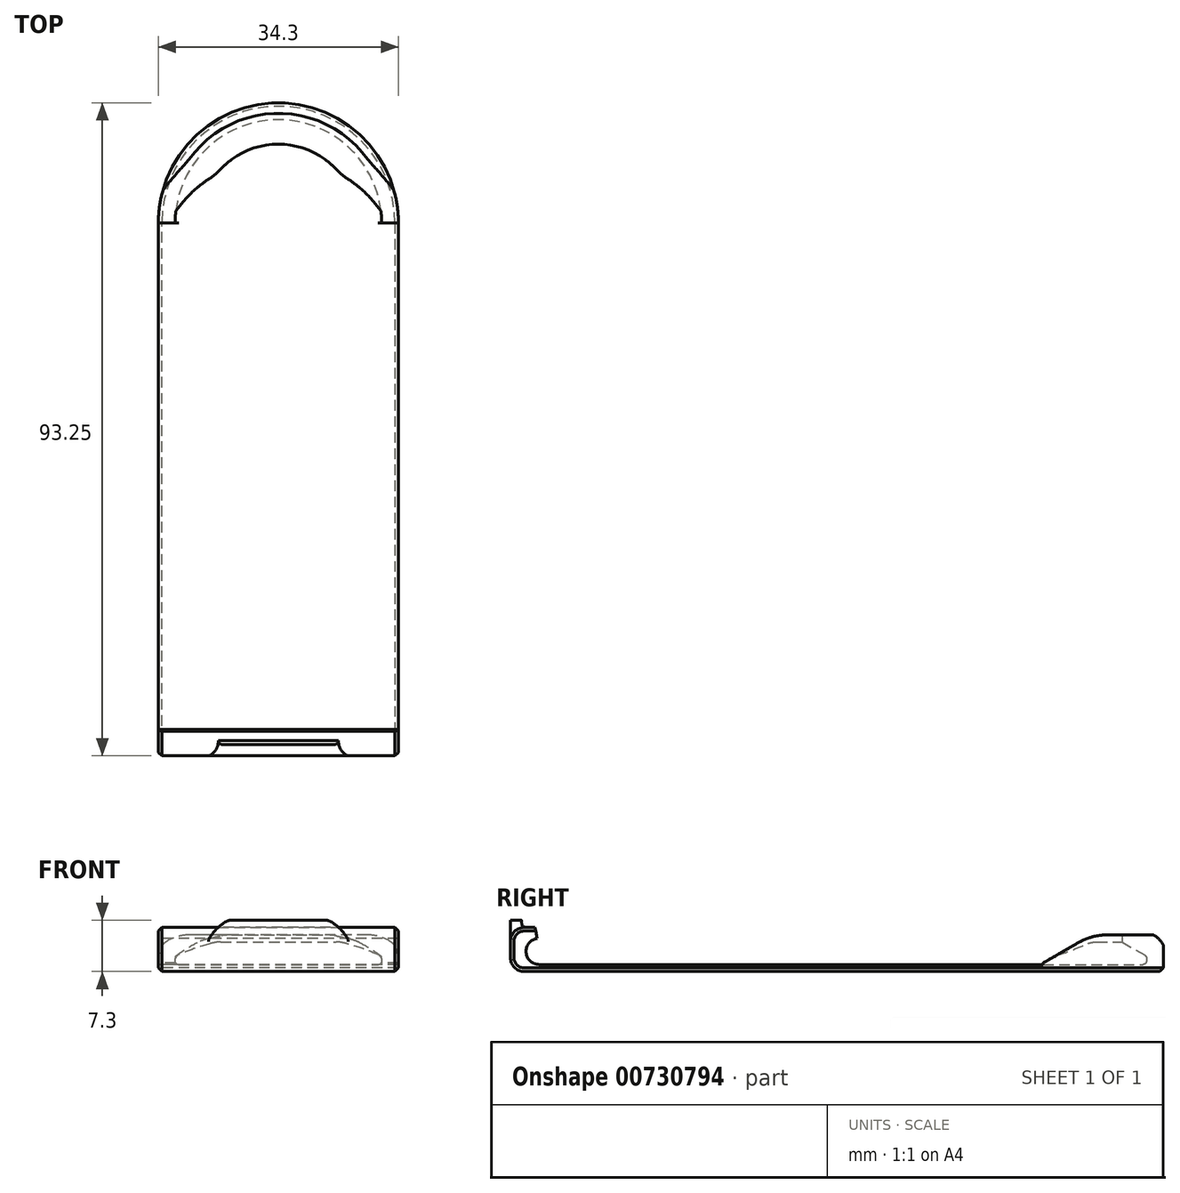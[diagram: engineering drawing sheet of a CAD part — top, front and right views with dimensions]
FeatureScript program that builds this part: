
annotation { "Feature Type Name" : "Feature", "Feature Type Description" : "" }
export const myFeature = defineFeature(function(context is Context, id is Id, definition is map)
    precondition{}
    {
        {
            var Q0;
            Q0=qCreatedBy(makeId("Front.planeOp"),FACE);
            var sketch = newSketch(context, id + "F0", { "sketchPlane" : qUnion([Q0])});
            skLineSegment(sketch, "E0", {"start": v(0, 0) * mm, "end": v(0, 1) * mm});
            skLineSegment(sketch, "E1", {"start": v(0, 1) * mm, "end": v(14.75, 1) * mm});
            skLineSegment(sketch, "E2", {"start": v(14.75, 1) * mm, "end": v(14.75, 2.2) * mm});
            skLineSegment(sketch, "E3", {"start": v(14.75, 2.2) * mm, "end": v(11.25, 4.22) * mm});
            skLineSegment(sketch, "E4", {"start": v(11.25, 4.22) * mm, "end": v(11.25, 5.22) * mm});
            skLineSegment(sketch, "E5", {"start": v(11.25, 5.22) * mm, "end": v(17.15, 5.22) * mm});
            skLineSegment(sketch, "E6", {"start": v(17.15, 5.22) * mm, "end": v(17.15, 0) * mm});
            skLineSegment(sketch, "E7", {"start": v(17.15, 0) * mm, "end": v(0, 0) * mm});
            skSolve(sketch);
        }
        {
            var Q0;
            Q0=makeQuery(id+"F0.imprint","IMPRINT",FACE,{"disambiguationData":[TD([[makeQuery(id+"F0.imprint","IMPRINT",EDGE,{"derivedFrom":sQuery(id+"F0.wireOp",EDGE,"E0")}),-1.0]])]});
            var Q1;
            Q1=sQuery(id+"F0.wireOp",EDGE,"E0");
            revolve(context, id + "F1", {"surfaceOperationType" : NewSurfaceOperationType.NEW, "entities" : qUnion([Q0]), "axis" : qUnion([Q1]), "revolveType" : RevolveType.ONE_DIRECTION, "angle" : 180 * degree});
        }
        {
            var Q0;
            Q0=qCreatedBy(makeId("Top.planeOp"),FACE);
            var sketch = newSketch(context, id + "F2", { "sketchPlane" : qUnion([Q0])});
            skLineSegment(sketch, "E8.bottom", {"start": v(-17.15, 0) * mm, "end": v(17.15, 0) * mm});
            skLineSegment(sketch, "E8.top", {"start": v(-17.15, -72) * mm, "end": v(17.15, -72) * mm});
            skLineSegment(sketch, "E8.left", {"start": v(-17.15, 0) * mm, "end": v(-17.15, -72) * mm});
            skLineSegment(sketch, "E8.right", {"start": v(17.15, 0) * mm, "end": v(17.15, -72) * mm});
            skSolve(sketch);
        }
        {
            var Q0;
            Q0=makeQuery(id+"F2.imprint","IMPRINT",FACE,{"disambiguationData":[TD([[makeQuery(id+"F2.imprint","IMPRINT",EDGE,{"derivedFrom":sQuery(id+"F2.wireOp",EDGE,"E8.bottom")}),-1.0]])]});
            var Q1;
            Q1=makeQuery(id+"F1.opRevolve","SWEPT_FACE",FACE,{"disambiguationData":[OSD([sQuery(id+"F0.wireOp",EDGE,"E1")])]});
            extrude(context, id + "F3", {"entities" : qUnion([Q0]), "operationType" : NewBodyOperationType.ADD, "endBound" : BoundingType.UP_TO_SURFACE, "depth" : 25 * mm, "endBoundEntityFace" : qUnion([Q1]), "offsetDistance" : 25 * mm});
        }
        {
            var Q0;
            {var subQ0=sQuery(id+"F0.wireOp",EDGE,"E1");Q0=makeQuery(id+"F3.boolean.opBoolean","MERGE",FACE,{"derivedFrom":[makeQuery(id+"F1.opRevolve","SWEPT_FACE",FACE,{"disambiguationData":[OSD([subQ0])]}),makeQuery(id+"F3.opExtrude","CAP_FACE",FACE,{"disambiguationData":[OSD([subQ0])],"isStart":false})]});}
            var sketch = newSketch(context, id + "F4", { "sketchPlane" : qUnion([Q0])});
            skCircle(sketch, "E9", {"center": v(0, 0) * mm, "radius": 14.75 * mm, "construction": true});
            skSolve(sketch);
        }
        {
            var Q0;
            Q0=makeQuery(id+"F1.opRevolve","CAP_EDGE",EDGE,{"disambiguationData":[OSD([sQuery(id+"F0.wireOp",EDGE,"E5")])],"isStart":false});
            var Q1;
            Q1=makeQuery(id+"F1.opRevolve","CAP_EDGE",EDGE,{"disambiguationData":[OSD([sQuery(id+"F0.wireOp",EDGE,"E5")])],"isStart":true});
            chamfer(context, id + "F5", {"entities" : qUnion([Q0, Q1]), "chamferType" : ChamferType.OFFSET_ANGLE, "width" : 4 * mm, "oppositeDirection" : false, "angle" : 60 * degree, "tangentPropagation" : true});
        }
        {
            var Q0;
            Q0=makeQuery(id+"F1.opRevolve","SWEPT_FACE",FACE,{"disambiguationData":[OSD([sQuery(id+"F0.wireOp",EDGE,"E5")])]});
            var sketch = newSketch(context, id + "F6", { "sketchPlane" : qUnion([Q0])});
            skArc(sketch, "E10", {"start": v(14.65, 1.7) * mm, "mid": v(0, 9.27) * mm, "end": v(-14.65, 1.7) * mm});
            skLineSegment(sketch, "E11", {"start": v(-14.65, 1.7) * mm, "end": v(14.65, 1.7) * mm});
            skSolve(sketch);
        }
        {
            var Q0;
            Q0 = qSketchRegion(id + "F6", true);
            var Q1;
            {var subQ0=sQuery(id+"F0.wireOp",EDGE,"E1");Q1=makeQuery(id+"F3.boolean.opBoolean","MERGE",FACE,{"derivedFrom":[makeQuery(id+"F1.opRevolve","SWEPT_FACE",FACE,{"disambiguationData":[OSD([subQ0])]}),makeQuery(id+"F3.opExtrude","CAP_FACE",FACE,{"disambiguationData":[OSD([subQ0])],"isStart":false})]});}
            extrude(context, id + "F7", {"entities" : qUnion([Q0]), "operationType" : NewBodyOperationType.REMOVE, "endBound" : BoundingType.UP_TO_SURFACE, "oppositeDirection" : true, "depth" : 25 * mm, "endBoundEntityFace" : qUnion([Q1]), "offsetDistance" : 25 * mm});
        }
        {
            var Q0;
            Q0=makeQuery(id+"F1.opRevolve","SWEPT_EDGE",EDGE,{"disambiguationData":[OSD([sQuery(id+"F0.wireOp",EDGE,"E2"),sQuery(id+"F0.wireOp",EDGE,"E3")])]});
            var Q1;
            Q1=makeQuery(id+"F1.opRevolve","SWEPT_EDGE",EDGE,{"disambiguationData":[OSD([sQuery(id+"F0.wireOp",EDGE,"E1"),sQuery(id+"F0.wireOp",EDGE,"E2")])]});
            fillet(context, id + "F8", {"entities" : qUnion([Q0, Q1]), "radius" : .5 * mm, "allowEdgeOverflow" : false});
        }
        {
            var Q0;
            Q0=makeQuery(id+"F3.opExtrude","SWEPT_FACE",FACE,{"disambiguationData":[OSD([sQuery(id+"F2.wireOp",EDGE,"E8.left")])]});
            var sketch = newSketch(context, id + "F9", { "sketchPlane" : qUnion([Q0])});
            skArc(sketch, "E12", {"start": v(72, 1) * mm, "mid": v(73.87, 2.71) * mm, "end": v(72.33, 4.72) * mm});
            skLineSegment(sketch, "E13", {"start": v(72.33, 4.72) * mm, "end": v(72.6, 6.3) * mm});
            skLineSegment(sketch, "E14", {"start": v(72.6, 6.3) * mm, "end": v(76.1, 6.3) * mm});
            skLineSegment(sketch, "E15", {"start": v(76.1, 6.3) * mm, "end": v(76.1, 0) * mm});
            skLineSegment(sketch, "E16", {"start": v(76.1, 0) * mm, "end": v(72, 0) * mm});
            skLineSegment(sketch, "E17", {"start": v(72, 0) * mm, "end": v(72, 1) * mm});
            skSolve(sketch);
        }
        {
            var Q0;
            Q0 = qSketchRegion(id + "F9", true);
            var Q1;
            Q1=makeQuery(id+"F3.opExtrude","SWEPT_FACE",FACE,{"disambiguationData":[OSD([sQuery(id+"F2.wireOp",EDGE,"E8.right")])]});
            extrude(context, id + "F10", {"entities" : qUnion([Q0]), "operationType" : NewBodyOperationType.ADD, "endBound" : BoundingType.UP_TO_SURFACE, "oppositeDirection" : true, "depth" : 25 * mm, "endBoundEntityFace" : qUnion([Q1]), "offsetDistance" : 25 * mm});
        }
        {
            var Q0;
            Q0=makeQuery(id+"F10.opExtrude","SWEPT_EDGE",EDGE,{"disambiguationData":[OSD([sQuery(id+"F9.wireOp",EDGE,"E14"),sQuery(id+"F9.wireOp",EDGE,"E15")])]});
            var Q1;
            Q1=makeQuery(id+"F10.opExtrude","SWEPT_EDGE",EDGE,{"disambiguationData":[OSD([sQuery(id+"F9.wireOp",EDGE,"E15"),sQuery(id+"F9.wireOp",EDGE,"E16")])]});
            fillet(context, id + "F11", {"entities" : qUnion([Q0, Q1]), "radius" : 2 * mm, "tangentPropagation" : true, "allowEdgeOverflow" : false});
        }
        {
            var Q0;
            Q0=makeQuery(id+"F1.opRevolve","SWEPT_EDGE",EDGE,{"disambiguationData":[OSD([sQuery(id+"F0.wireOp",EDGE,"E5"),sQuery(id+"F0.wireOp",EDGE,"E6")])]});
            fillet(context, id + "F12", {"entities" : qUnion([Q0]), "radius" : 1.5 * mm, "tangentPropagation" : true, "rho" : .2, "crossSection" : FilletCrossSection.CONIC, "allowEdgeOverflow" : false});
        }
        {
            var Q0;
            {var subQ0=sQuery(id+"F0.wireOp",EDGE,"E5");Q0=makeQuery(id+"F5.opChamfer","BLEND_EDGE",EDGE,{"blendedFrom":[makeQuery(id+"F1.opRevolve","CAP_EDGE",EDGE,{"disambiguationData":[OSD([subQ0])],"isStart":true}),makeQuery(id+"F1.opRevolve","SWEPT_FACE",FACE,{"disambiguationData":[OSD([subQ0])]})],"blendedInto":[makeQuery(id+"F1.opRevolve","SWEPT_FACE",FACE,{"disambiguationData":[OSD([subQ0])]})]});}
            var Q1;
            {var subQ0=sQuery(id+"F0.wireOp",EDGE,"E1");Q1=makeQuery(id+"F5.opChamfer","BLEND_EDGE",EDGE,{"blendedFrom":[makeQuery(id+"F1.opRevolve","CAP_EDGE",EDGE,{"disambiguationData":[OSD([sQuery(id+"F0.wireOp",EDGE,"E5")])],"isStart":true}),makeQuery(id+"F3.boolean.opBoolean","MERGE",FACE,{"derivedFrom":[makeQuery(id+"F1.opRevolve","SWEPT_FACE",FACE,{"disambiguationData":[OSD([subQ0])]}),makeQuery(id+"F3.opExtrude","CAP_FACE",FACE,{"disambiguationData":[OSD([subQ0])],"isStart":false})]})],"blendedInto":[makeQuery(id+"F3.boolean.opBoolean","MERGE",FACE,{"derivedFrom":[makeQuery(id+"F1.opRevolve","SWEPT_FACE",FACE,{"disambiguationData":[OSD([subQ0])]}),makeQuery(id+"F3.opExtrude","CAP_FACE",FACE,{"disambiguationData":[OSD([subQ0])],"isStart":false})]})]});}
            var Q2;
            {var subQ0=sQuery(id+"F0.wireOp",EDGE,"E1");Q2=makeQuery(id+"F5.opChamfer","BLEND_EDGE",EDGE,{"blendedFrom":[makeQuery(id+"F1.opRevolve","CAP_EDGE",EDGE,{"disambiguationData":[OSD([sQuery(id+"F0.wireOp",EDGE,"E5")])],"isStart":false}),makeQuery(id+"F3.boolean.opBoolean","MERGE",FACE,{"derivedFrom":[makeQuery(id+"F1.opRevolve","SWEPT_FACE",FACE,{"disambiguationData":[OSD([subQ0])]}),makeQuery(id+"F3.opExtrude","CAP_FACE",FACE,{"disambiguationData":[OSD([subQ0])],"isStart":false})]})],"blendedInto":[makeQuery(id+"F3.boolean.opBoolean","MERGE",FACE,{"derivedFrom":[makeQuery(id+"F1.opRevolve","SWEPT_FACE",FACE,{"disambiguationData":[OSD([subQ0])]}),makeQuery(id+"F3.opExtrude","CAP_FACE",FACE,{"disambiguationData":[OSD([subQ0])],"isStart":false})]})]});}
            var Q3;
            {var subQ0=sQuery(id+"F0.wireOp",EDGE,"E5");Q3=makeQuery(id+"F5.opChamfer","BLEND_EDGE",EDGE,{"blendedFrom":[makeQuery(id+"F1.opRevolve","CAP_EDGE",EDGE,{"disambiguationData":[OSD([subQ0])],"isStart":false}),makeQuery(id+"F1.opRevolve","SWEPT_FACE",FACE,{"disambiguationData":[OSD([subQ0])]})],"blendedInto":[makeQuery(id+"F1.opRevolve","SWEPT_FACE",FACE,{"disambiguationData":[OSD([subQ0])]})]});}
            var Q4;
            Q4=makeQuery(id+"F7.boolean.opBoolean","INTERSECT",EDGE,{"disambiguationData":[OD(1.0)],"derivedFrom":[makeQuery(id+"F1.opRevolve","SWEPT_FACE",FACE,{"disambiguationData":[OSD([sQuery(id+"F0.wireOp",EDGE,"E4")])]}),makeQuery(id+"F7.opExtrude","SWEPT_FACE",FACE,{"disambiguationData":[OSD([sQuery(id+"F6.wireOp",EDGE,"E10")])]})]});
            var Q5;
            Q5=makeQuery(id+"F7.boolean.opBoolean","INTERSECT",EDGE,{"disambiguationData":[OD(0.0)],"derivedFrom":[makeQuery(id+"F1.opRevolve","SWEPT_FACE",FACE,{"disambiguationData":[OSD([sQuery(id+"F0.wireOp",EDGE,"E4")])]}),makeQuery(id+"F7.opExtrude","SWEPT_FACE",FACE,{"disambiguationData":[OSD([sQuery(id+"F6.wireOp",EDGE,"E10")])]})]});
            fillet(context, id + "F13", {"entities" : qUnion([Q0, Q1, Q2, Q3, Q4, Q5]), "radius" : 8 * mm, "allowEdgeOverflow" : false});
        }
        {
            var Q0;
            Q0=makeQuery(id+"F10.opExtrude","SWEPT_FACE",FACE,{"disambiguationData":[OSD([sQuery(id+"F9.wireOp",EDGE,"E15")])]});
            var sketch = newSketch(context, id + "F14", { "sketchPlane" : qUnion([Q0])});
            skLineSegment(sketch, "E18", {"start": v(-10, 4.3) * mm, "end": v(-10, 7.3) * mm});
            skLineSegment(sketch, "E19", {"start": v(-10, 7.3) * mm, "end": v(10, 7.3) * mm});
            skLineSegment(sketch, "E20", {"start": v(10, 7.3) * mm, "end": v(10, 4.3) * mm});
            skLineSegment(sketch, "E21", {"start": v(10, 4.3) * mm, "end": v(-10, 4.3) * mm});
            skPoint(sketch, "E22", {"position": v(0, 0) * mm});
            skSolve(sketch);
        }
        {
            var Q0;
            Q0 = qSketchRegion(id + "F14", true);
            extrude(context, id + "F15", {"entities" : qUnion([Q0]), "operationType" : NewBodyOperationType.ADD, "oppositeDirection" : true, "depth" : 1.6 * mm, "offsetDistance" : 25 * mm});
        }
        {
            var Q0;
            Q0=makeQuery(id+"F15.opExtrude","SWEPT_EDGE",EDGE,{"disambiguationData":[OSD([sQuery(id+"F14.wireOp",EDGE,"E19"),sQuery(id+"F14.wireOp",EDGE,"E20")])]});
            var Q1;
            Q1=makeQuery(id+"F15.opExtrude","SWEPT_EDGE",EDGE,{"disambiguationData":[OSD([sQuery(id+"F14.wireOp",EDGE,"E18"),sQuery(id+"F14.wireOp",EDGE,"E19")])]});
            fillet(context, id + "F16", {"entities" : qUnion([Q0, Q1]), "radius" : 3 * mm, "tangentPropagation" : true, "rho" : .2, "crossSection" : FilletCrossSection.CONIC, "allowEdgeOverflow" : false});
        }
        {
            var Q0;
            Q0=makeQuery(id+"F15.boolean.opBoolean","INTERSECT",EDGE,{"derivedFrom":[makeQuery(id+"F11.opFillet","BLEND_FACE",FACE,{"disambiguationData":[OSD([sQuery(id+"F9.wireOp",EDGE,"E14"),sQuery(id+"F9.wireOp",EDGE,"E15")])]}),makeQuery(id+"F15.opExtrude","CAP_FACE",FACE,{"disambiguationData":[OSD([sQuery(id+"F14.wireOp",EDGE,"E18"),sQuery(id+"F14.wireOp",EDGE,"E19"),sQuery(id+"F14.wireOp",EDGE,"E20"),sQuery(id+"F14.wireOp",EDGE,"E21")])],"isStart":false})]});
            fillet(context, id + "F17", {"entities" : qUnion([Q0]), "radius" : 1 * mm, "tangentPropagation" : true, "rho" : .7, "crossSection" : FilletCrossSection.CONIC, "allowEdgeOverflow" : false});
        }
        {
            var Q0;
            Q0=makeQuery(id+"F1.opRevolve","SWEPT_EDGE",EDGE,{"disambiguationData":[OSD([sQuery(id+"F0.wireOp",EDGE,"E6"),sQuery(id+"F0.wireOp",EDGE,"E7")])]});
            chamfer(context, id + "F18", {"entities" : qUnion([Q0]), "width" : .5 * mm, "tangentPropagation" : true});
        }
    });
